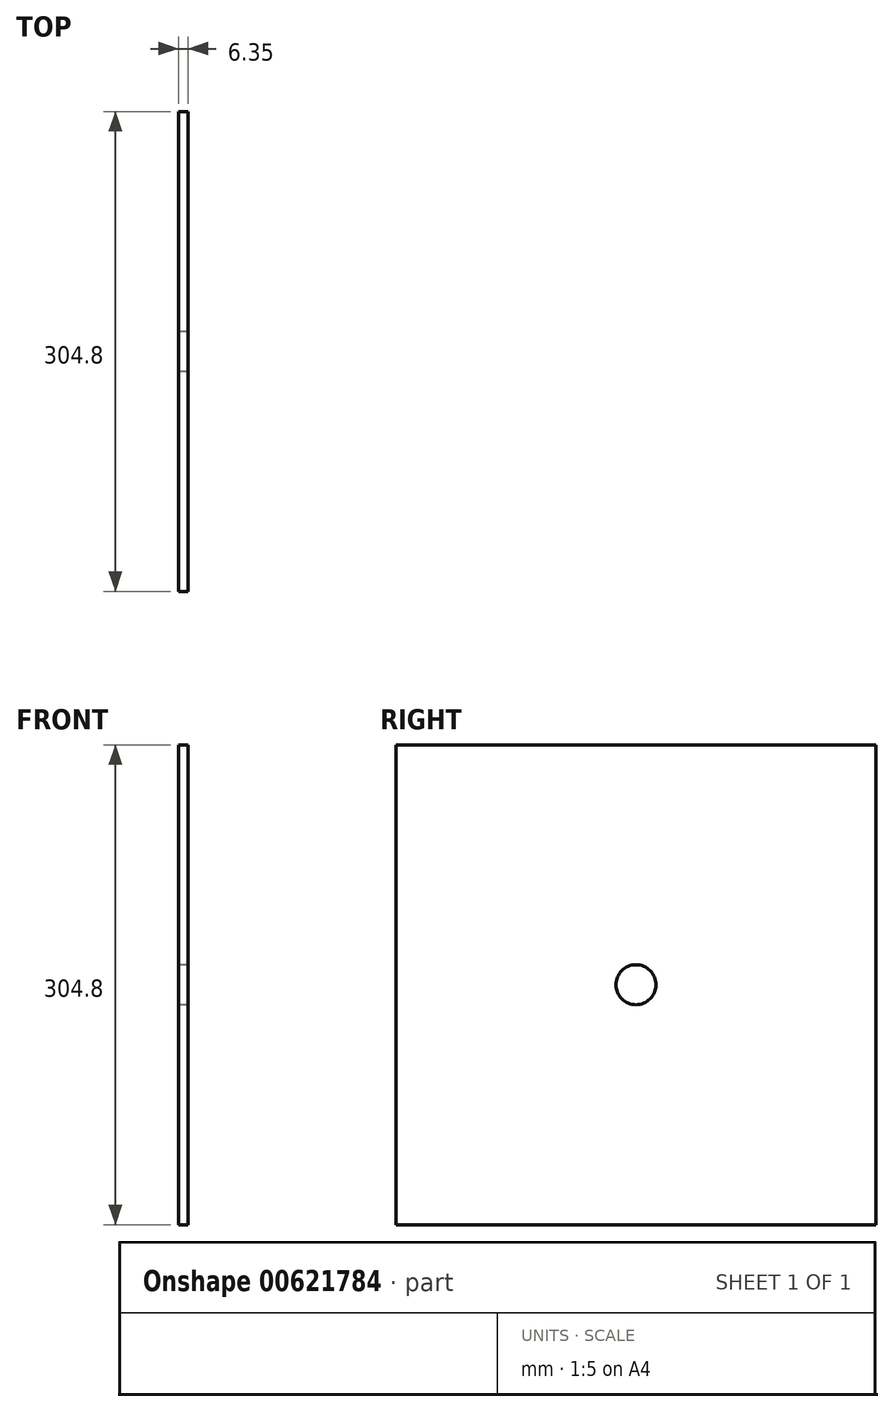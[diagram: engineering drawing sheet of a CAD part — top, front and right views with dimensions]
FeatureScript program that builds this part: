
annotation { "Feature Type Name" : "Feature", "Feature Type Description" : "" }
export const myFeature = defineFeature(function(context is Context, id is Id, definition is map)
    precondition{}
    {
        {
            var Q0;
            Q0=qCreatedBy(makeId("Right.planeOp"),FACE);
            var sketch = newSketch(context, id + "F0", { "sketchPlane" : qUnion([Q0])});
            skLineSegment(sketch, "E0.bottom", {"start": v(152.4, -152.4) * mm, "end": v(-152.4, -152.4) * mm});
            skLineSegment(sketch, "E0.top", {"start": v(152.4, 152.4) * mm, "end": v(-152.4, 152.4) * mm});
            skLineSegment(sketch, "E0.left", {"start": v(152.4, -152.4) * mm, "end": v(152.4, 152.4) * mm});
            skLineSegment(sketch, "E0.right", {"start": v(-152.4, -152.4) * mm, "end": v(-152.4, 152.4) * mm});
            skPoint(sketch, "E0.middle", {"position": v(0, 0) * mm});
            skCircle(sketch, "E1", {"center": v(0, 0) * mm, "radius": 12.7 * mm});
            skSolve(sketch);
        }
        {
            var Q0;
            Q0=makeQuery(id+"F0.imprint","IMPRINT",FACE,{"disambiguationData":[TD([[makeQuery(id+"F0.imprint","IMPRINT",EDGE,{"derivedFrom":sQuery(id+"F0.wireOp",EDGE,"E0.bottom")}),-1.0]])]});
            extrude(context, id + "F1", {"entities" : qUnion([Q0]), "depth" : 6.35 * mm, "offsetDistance" : 25.4 * mm});
        }
    });
